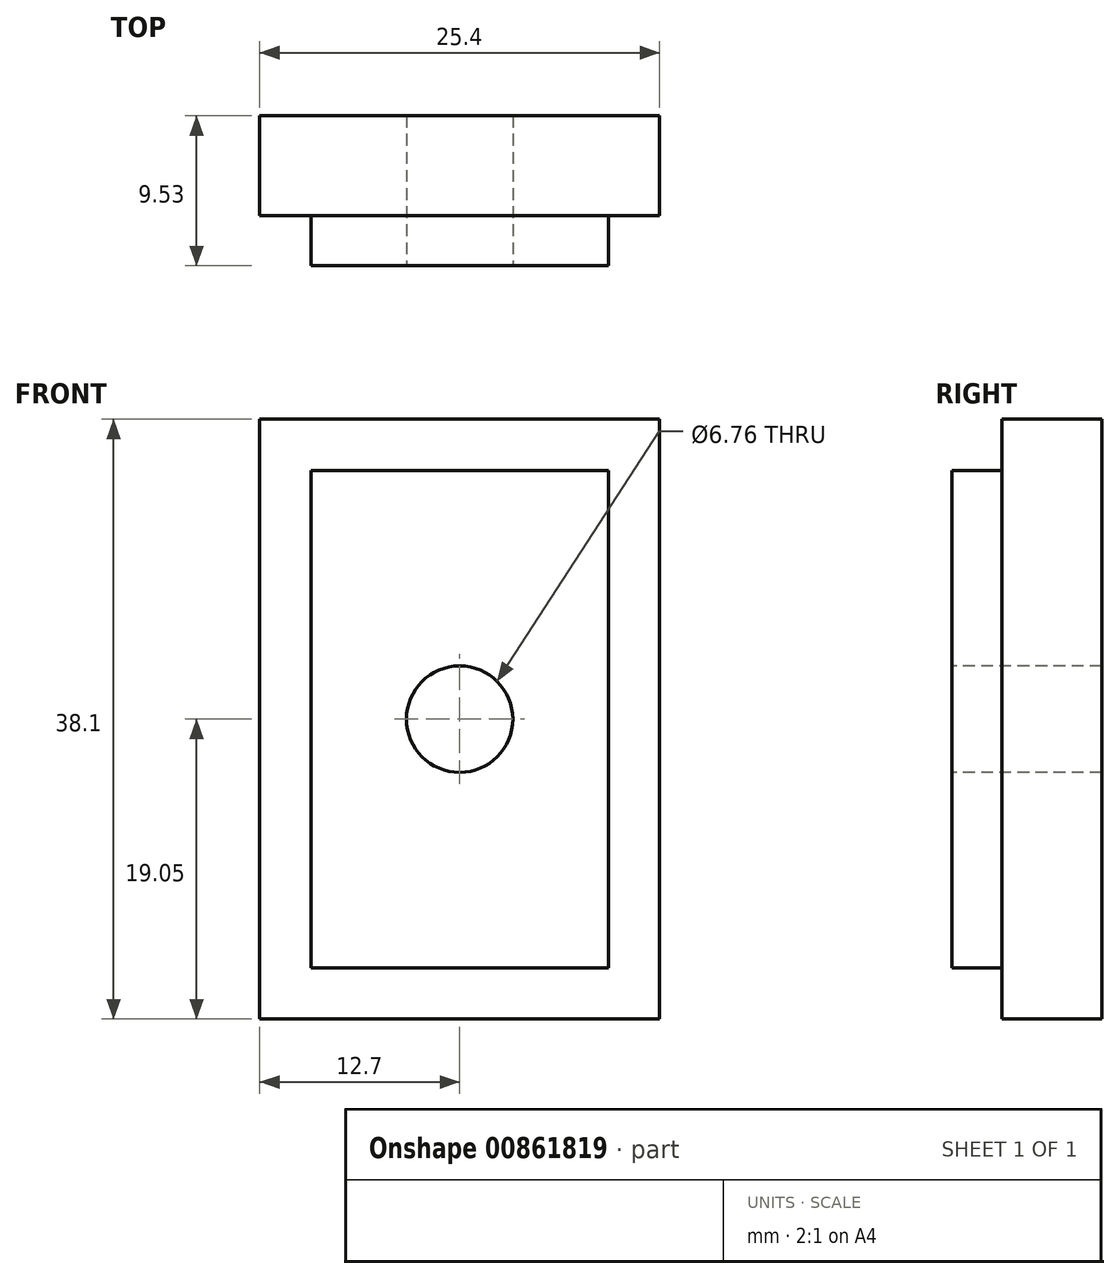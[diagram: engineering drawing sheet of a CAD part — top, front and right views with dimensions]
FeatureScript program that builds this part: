
annotation { "Feature Type Name" : "Feature", "Feature Type Description" : "" }
export const myFeature = defineFeature(function(context is Context, id is Id, definition is map)
    precondition{}
    {
        {
            var Q0;
            Q0=qCreatedBy(makeId("Front.planeOp"),FACE);
            var sketch = newSketch(context, id + "F0", { "sketchPlane" : qUnion([Q0])});
            skLineSegment(sketch, "E0.bottom", {"start": v(0, 0) * mm, "end": v(25.4, 0) * mm});
            skLineSegment(sketch, "E0.top", {"start": v(0, 38.1) * mm, "end": v(25.4, 38.1) * mm});
            skLineSegment(sketch, "E0.left", {"start": v(0, 0) * mm, "end": v(0, 38.1) * mm});
            skLineSegment(sketch, "E0.right", {"start": v(25.4, 0) * mm, "end": v(25.4, 38.1) * mm});
            skSolve(sketch);
        }
        {
            var Q0;
            Q0=makeQuery(id+"F0.imprint","IMPRINT",FACE,{"disambiguationData":[TD([[makeQuery(id+"F0.imprint","IMPRINT",EDGE,{"derivedFrom":sQuery(id+"F0.wireOp",EDGE,"E0.bottom")}),1.0]])]});
            extrude(context, id + "F1", {"entities" : qUnion([Q0]), "oppositeDirection" : true, "depth" : 6.35 * mm, "offsetDistance" : 25.4 * mm});
        }
        {
            var Q0;
            Q0=makeQuery(id+"F1.opExtrude","CAP_FACE",FACE,{"disambiguationData":[OSD([sQuery(id+"F0.wireOp",EDGE,"E0.bottom"),sQuery(id+"F0.wireOp",EDGE,"E0.top"),sQuery(id+"F0.wireOp",EDGE,"E0.left"),sQuery(id+"F0.wireOp",EDGE,"E0.right")])],"isStart":true});
            var sketch = newSketch(context, id + "F2", { "sketchPlane" : qUnion([Q0])});
            skLineSegment(sketch, "E1.0", {"start": v(3.25, 34.85) * mm, "end": v(22.15, 34.85) * mm});
            skLineSegment(sketch, "E1.1", {"start": v(3.25, 3.25) * mm, "end": v(3.25, 34.85) * mm});
            skLineSegment(sketch, "E1.2", {"start": v(3.25, 3.25) * mm, "end": v(22.15, 3.25) * mm});
            skLineSegment(sketch, "E1.3", {"start": v(22.15, 3.25) * mm, "end": v(22.15, 34.85) * mm});
            skSolve(sketch);
        }
        {
            var Q0;
            Q0=makeQuery(id+"F2.imprint","IMPRINT",FACE,{"disambiguationData":[TD([[makeQuery(id+"F2.imprint","IMPRINT",EDGE,{"derivedFrom":sQuery(id+"F2.wireOp",EDGE,"E1.0")}),-1.0]])]});
            extrude(context, id + "F3", {"entities" : qUnion([Q0]), "operationType" : NewBodyOperationType.ADD, "depth" : 3.17 * mm, "offsetDistance" : 25.4 * mm});
        }
        {
            var Q0;
            Q0=makeQuery(id+"F3.opExtrude","CAP_FACE",FACE,{"disambiguationData":[OSD([sQuery(id+"F2.wireOp",EDGE,"E1.0"),sQuery(id+"F2.wireOp",EDGE,"E1.1"),sQuery(id+"F2.wireOp",EDGE,"E1.2"),sQuery(id+"F2.wireOp",EDGE,"E1.3")])],"isStart":false});
            var sketch = newSketch(context, id + "F4", { "sketchPlane" : qUnion([Q0])});
            skCircle(sketch, "E2", {"center": v(12.7, 19.05) * mm, "radius": 3.38 * mm});
            skSolve(sketch);
        }
        {
            var Q0;
            Q0=makeQuery(id+"F4.imprint","IMPRINT",FACE,{"disambiguationData":[TD([[makeQuery(id+"F4.imprint","IMPRINT",EDGE,{"derivedFrom":sQuery(id+"F4.wireOp",EDGE,"E2")}),1.0]])]});
            extrude(context, id + "F5", {"entities" : qUnion([Q0]), "operationType" : NewBodyOperationType.REMOVE, "oppositeDirection" : true, "depth" : 25.4 * mm, "offsetDistance" : 25.4 * mm});
        }
    });
